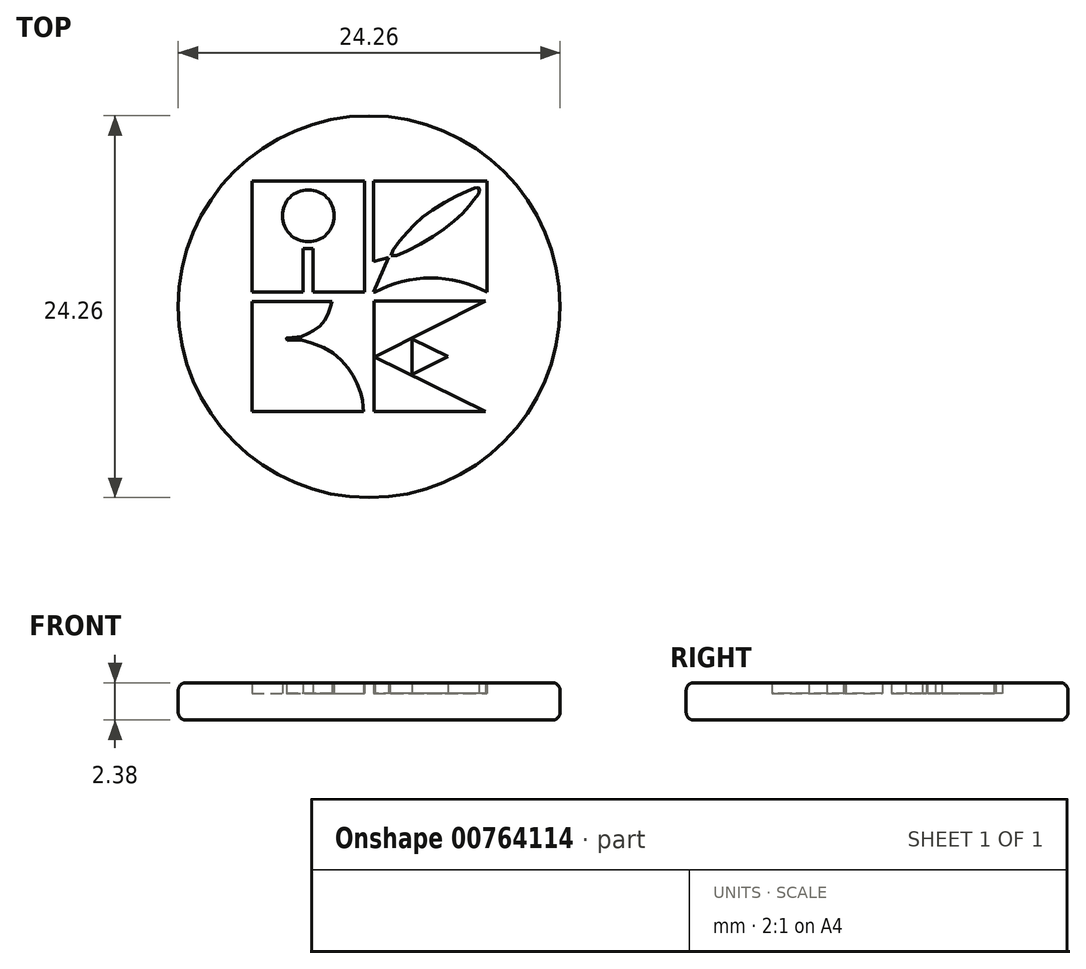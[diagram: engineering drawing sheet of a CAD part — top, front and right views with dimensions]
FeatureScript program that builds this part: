
annotation { "Feature Type Name" : "Feature", "Feature Type Description" : "" }
export const myFeature = defineFeature(function(context is Context, id is Id, definition is map)
    precondition{}
    {
        {
            assignVariable(context, id + "F0", {"name" : "SPES", "anyValue" : 2.38});
        }
        {
            var Q0;
            Q0=qCreatedBy(makeId("Top.planeOp"),FACE);
            var sketch = newSketch(context, id + "F1", { "sketchPlane" : qUnion([Q0])});
            skCircle(sketch, "E0", {"center": v(0, 0) * mm, "radius": 12.12 * mm});
            skLineSegment(sketch, "E1.bottom", {"start": v(-7.42, 7.97) * mm, "end": v(-0.28, 7.97) * mm});
            skLineSegment(sketch, "E1.top", {"start": v(-7.42, 0.93) * mm, "end": v(-4.19, 0.93) * mm});
            skLineSegment(sketch, "E1.left", {"start": v(-7.42, 7.97) * mm, "end": v(-7.42, 0.93) * mm});
            skLineSegment(sketch, "E1.right", {"start": v(-0.28, 7.97) * mm, "end": v(-0.28, 0.93) * mm});
            skLineSegment(sketch, "E2.bottom", {"start": v(-7.42, 0.33) * mm, "end": v(-0.28, 0.33) * mm});
            skLineSegment(sketch, "E2.top", {"start": v(-7.42, -6.67) * mm, "end": v(-0.28, -6.67) * mm});
            skLineSegment(sketch, "E2.left", {"start": v(-7.42, 0.33) * mm, "end": v(-7.42, -6.67) * mm});
            skLineSegment(sketch, "E2.right", {"start": v(-0.28, 0.33) * mm, "end": v(-0.28, -6.67) * mm});
            skLineSegment(sketch, "E3.bottom", {"start": v(0.3, 0.35) * mm, "end": v(7.4, 0.35) * mm});
            skLineSegment(sketch, "E3.top", {"start": v(0.3, -6.67) * mm, "end": v(7.4, -6.67) * mm});
            skLineSegment(sketch, "E3.left", {"start": v(0.3, 0.35) * mm, "end": v(0.3, -6.67) * mm});
            skLineSegment(sketch, "E3.right", {"start": v(7.4, 0.35) * mm, "end": v(7.4, -6.67) * mm});
            skLineSegment(sketch, "E4.bottom", {"start": v(0.28, 7.97) * mm, "end": v(7.48, 7.97) * mm});
            skLineSegment(sketch, "E4.top", {"start": v(0.28, 0.93) * mm, "end": v(7.48, 0.93) * mm});
            skLineSegment(sketch, "E4.left", {"start": v(0.28, 7.97) * mm, "end": v(0.28, 0.93) * mm});
            skLineSegment(sketch, "E4.right", {"start": v(7.48, 7.97) * mm, "end": v(7.48, 0.93) * mm});
            skCircle(sketch, "E5", {"center": v(-3.86, 5.78) * mm, "radius": 1.65 * mm});
            skPoint(sketch, "E5.first.point", {"position": v(-3.9, 7.42) * mm});
            skPoint(sketch, "E5.second.point", {"position": v(-2.22, 5.67) * mm});
            skPoint(sketch, "E5.third.point", {"position": v(-5.51, 5.72) * mm});
            skLineSegment(sketch, "E6.bottom", {"start": v(-4.19, 3.7) * mm, "end": v(-3.57, 3.7) * mm});
            skLineSegment(sketch, "E6.left", {"start": v(-4.19, 3.7) * mm, "end": v(-4.19, 0.93) * mm});
            skLineSegment(sketch, "E6.right", {"start": v(-3.57, 3.7) * mm, "end": v(-3.57, 0.93) * mm});
            skLineSegment(sketch, "E7.trimOffspring", {"start": v(-3.57, 0.93) * mm, "end": v(-0.28, 0.93) * mm});
            skLineSegment(sketch, "E8", {"start": v(-4.19, 0.93) * mm, "end": v(-3.57, 0.93) * mm});
            skLineSegment(sketch, "E9", {"start": v(7.4, 0.35) * mm, "end": v(0.35, -3.18) * mm});
            skLineSegment(sketch, "E10", {"start": v(0.35, -3.18) * mm, "end": v(7.4, -6.67) * mm});
            skLineSegment(sketch, "E11", {"start": v(2.73, -2.04) * mm, "end": v(2.73, -4.31) * mm});
            skLineSegment(sketch, "E12", {"start": v(2.73, -4.31) * mm, "end": v(5, -3.17) * mm});
            skLineSegment(sketch, "E13", {"start": v(5, -3.17) * mm, "end": v(2.73, -2.04) * mm});
            skFitSpline(sketch, "E14", {"points": [v(1.38, 3.27) * mm, v(2.23, 4.5) * mm, v(3.76, 5.97) * mm, v(6.37, 7.42) * mm, v(6.9, 7.57) * mm, v(6.96, 7.53) * mm, v(7.02, 7.38) * mm, v(6.73, 6.87) * mm, v(5.74, 5.75) * mm, v(3.16, 3.91) * mm, v(1.38, 3.27) * mm]});
            skArc(sketch, "E15", {"start": v(7.48, 0.93) * mm, "mid": v(3.92, 1.83) * mm, "end": v(0.36, 0.93) * mm});
            skLineSegment(sketch, "E16", {"start": v(0.28, 0.93) * mm, "end": v(1.22, 3.12) * mm});
            skLineSegment(sketch, "E17", {"start": v(1.22, 3.12) * mm, "end": v(0.28, 2.89) * mm});
            skFitSpline(sketch, "E18", {"points": [v(-2.37, 0.33) * mm, v(-2.47, -0.07) * mm, v(-2.6, -0.45) * mm, v(-2.9, -0.95) * mm, v(-3.19, -1.28) * mm, v(-3.7, -1.6) * mm, v(-4, -1.79) * mm, v(-4.67, -1.97) * mm, v(-5.24, -1.98) * mm, v(-5.25, -2.04) * mm, v(-5.23, -2.1) * mm, v(-5.15, -2.13) * mm, v(-4.74, -2.1) * mm, v(-4.18, -2.15) * mm, v(-2.83, -2.63) * mm, v(-1.92, -3.27) * mm, v(-1.2, -4.1) * mm, v(-0.83, -4.73) * mm, v(-0.5, -5.55) * mm, v(-0.41, -6.06) * mm, v(-0.36, -6.5) * mm, v(-0.35, -6.67) * mm], "startDerivative": vector(-2.3, -9.32) * mm, "endDerivative": vector(0.32, -5.36) * mm});
            skSolve(sketch);
        }
        {
            var Q0;
            Q0=makeQuery(id+"F1.imprint","IMPRINT",FACE,{"disambiguationData":[TD([[makeQuery(id+"F1.imprint","IMPRINT",EDGE,{"derivedFrom":sQuery(id+"F1.wireOp",EDGE,"E0")}),1.0]])]});
            extrude(context, id + "F2", {"entities" : qUnion([Q0]), "depth" : (getVariable(context, 'SPES')) * mm, "offsetDistance" : 25 * mm});
        }
        {
            var Q0;
            Q0=makeQuery(id+"F2.opExtrude","CAP_EDGE",EDGE,{"disambiguationData":[OSD([sQuery(id+"F1.wireOp",EDGE,"E0")])],"isStart":false});
            fillet(context, id + "F3", {"entities" : qUnion([Q0]), "radius" : 0.5 * mm, "tangentPropagation" : true, "allowEdgeOverflow" : false});
        }
        {
            var Q0;
            Q0=makeQuery(id+"F2.opExtrude","CAP_EDGE",EDGE,{"disambiguationData":[OSD([sQuery(id+"F1.wireOp",EDGE,"E0")])],"isStart":true});
            fillet(context, id + "F4", {"entities" : qUnion([Q0]), "radius" : 0.5 * mm, "tangentPropagation" : true, "allowEdgeOverflow" : false});
        }
        {
            var Q0;
            Q0=makeQuery(id+"F1.imprint","IMPRINT",FACE,{"disambiguationData":[TD([[makeQuery(id+"F1.imprint","IMPRINT",EDGE,{"derivedFrom":sQuery(id+"F1.wireOp",EDGE,"E6.bottom")}),-1.0]])]});
            var Q1;
            Q1=makeQuery(id+"F1.imprint","IMPRINT",FACE,{"disambiguationData":[TD([[makeQuery(id+"F1.imprint","IMPRINT",EDGE,{"derivedFrom":sQuery(id+"F1.wireOp",EDGE,"E1.bottom")}),-1.0]])]});
            var Q2;
            Q2=makeQuery(id+"F1.imprint","IMPRINT",FACE,{"disambiguationData":[TD([[makeQuery(id+"F1.imprint","IMPRINT",EDGE,{"derivedFrom":sQuery(id+"F1.wireOp",EDGE,"E5")}),1.0]])]});
            extrude(context, id + "F5", {"entities" : qUnion([Q0, Q1, Q2]), "operationType" : NewBodyOperationType.ADD, "depth" : 1.7 * mm, "offsetDistance" : 25 * mm});
        }
        {
            var Q0;
            Q0=makeQuery(id+"F1.imprint","IMPRINT",FACE,{"disambiguationData":[TD([[makeQuery(id+"F1.imprint","IMPRINT",EDGE,{"derivedFrom":sQuery(id+"F1.wireOp",EDGE,"E5")}),1.0]])]});
            var Q1;
            Q1=makeQuery(id+"F1.imprint","IMPRINT",FACE,{"disambiguationData":[TD([[makeQuery(id+"F1.imprint","IMPRINT",EDGE,{"derivedFrom":sQuery(id+"F1.wireOp",EDGE,"E6.bottom")}),-1.0]])]});
            var Q2;
            Q2=makeQuery(id+"F2.opExtrude","CAP_FACE",FACE,{"disambiguationData":[OSD([sQuery(id+"F1.wireOp",EDGE,"E0"),sQuery(id+"F1.wireOp",EDGE,"E1.bottom"),sQuery(id+"F1.wireOp",EDGE,"E1.top"),sQuery(id+"F1.wireOp",EDGE,"E1.left"),sQuery(id+"F1.wireOp",EDGE,"E1.right"),sQuery(id+"F1.wireOp",EDGE,"E2.bottom"),sQuery(id+"F1.wireOp",EDGE,"E2.top"),sQuery(id+"F1.wireOp",EDGE,"E2.left"),sQuery(id+"F1.wireOp",EDGE,"E2.right"),sQuery(id+"F1.wireOp",EDGE,"E3.bottom"),sQuery(id+"F1.wireOp",EDGE,"E3.top"),sQuery(id+"F1.wireOp",EDGE,"E3.left"),sQuery(id+"F1.wireOp",EDGE,"E3.right"),sQuery(id+"F1.wireOp",EDGE,"E4.bottom"),sQuery(id+"F1.wireOp",EDGE,"E4.top"),sQuery(id+"F1.wireOp",EDGE,"E4.left"),sQuery(id+"F1.wireOp",EDGE,"E4.right"),sQuery(id+"F1.wireOp",EDGE,"E7.trimOffspring"),sQuery(id+"F1.wireOp",EDGE,"E8")])],"isStart":false});
            extrude(context, id + "F6", {"entities" : qUnion([Q0, Q1]), "operationType" : NewBodyOperationType.ADD, "endBound" : BoundingType.UP_TO_SURFACE, "depth" : 2 * mm, "endBoundEntityFace" : qUnion([Q2]), "offsetDistance" : 25 * mm});
        }
        {
            var Q0;
            {var subQ0=sQuery(id+"F1.wireOp",EDGE,"E3.bottom");Q0=makeQuery(id+"F1.imprint","IMPRINT",FACE,{"disambiguationData":[TD([[makeQuery(id+"F1.imprint","IMPRINT",EDGE,{"derivedFrom":subQ0}),-1.0]])]});}
            var Q1;
            {var subQ1=sQuery(id+"F1.wireOp",EDGE,"E3.right");Q1=makeQuery(id+"F1.imprint","IMPRINT",FACE,{"disambiguationData":[TD([[makeQuery(id+"F1.imprint","IMPRINT",EDGE,{"derivedFrom":subQ1}),-1.0]])]});}
            var Q2;
            Q2=makeQuery(id+"F1.imprint","IMPRINT",FACE,{"disambiguationData":[TD([[makeQuery(id+"F1.imprint","IMPRINT",EDGE,{"derivedFrom":sQuery(id+"F1.wireOp",EDGE,"IOD86GQd-rjmQ-qHtz-Bk1f-0n8stFa7D3gi")}),1.0]])]});
            var Q3;
            {var subQ0=sQuery(id+"F1.wireOp",EDGE,"E3.top");Q3=makeQuery(id+"F1.imprint","IMPRINT",FACE,{"disambiguationData":[TD([[makeQuery(id+"F1.imprint","IMPRINT",EDGE,{"derivedFrom":subQ0}),1.0]])]});}
            var Q4;
            {var subQ3=sQuery(id+"F1.wireOp",EDGE,"IOD86GQd-rjmQ-qHtz-Bk1f-0n8stFa7D3gi");Q4=makeQuery(id+"F1.imprint","IMPRINT",FACE,{"disambiguationData":[TD([[makeQuery(id+"F1.imprint","IMPRINT",EDGE,{"derivedFrom":subQ3}),-1.0]])]});}
            var Q5;
            Q5=makeQuery(id+"F1.imprint","IMPRINT",FACE,{"disambiguationData":[TD([[makeQuery(id+"F1.imprint","IMPRINT",EDGE,{"derivedFrom":sQuery(id+"F1.wireOp",EDGE,"E11")}),1.0]])]});
            extrude(context, id + "F7", {"entities" : qUnion([Q0, Q1, Q2, Q3, Q4, Q5]), "operationType" : NewBodyOperationType.ADD, "depth" : 1.7 * mm, "offsetDistance" : 25 * mm});
        }
        {
            var Q0;
            Q0=makeQuery(id+"F1.imprint","IMPRINT",FACE,{"disambiguationData":[TD([[makeQuery(id+"F1.imprint","IMPRINT",EDGE,{"derivedFrom":sQuery(id+"F1.wireOp",EDGE,"E3.right")}),-1.0]])]});
            var Q1;
            {var subQ0=sQuery(id+"F1.wireOp",EDGE,"E8");var subQ1=sQuery(id+"F1.wireOp",EDGE,"E7.trimOffspring");var subQ2=sQuery(id+"F1.wireOp",EDGE,"E4.right");var subQ3=sQuery(id+"F1.wireOp",EDGE,"E4.left");var subQ4=sQuery(id+"F1.wireOp",EDGE,"E4.top");var subQ5=sQuery(id+"F1.wireOp",EDGE,"E4.bottom");var subQ6=sQuery(id+"F1.wireOp",EDGE,"E3.right");var subQ7=sQuery(id+"F1.wireOp",EDGE,"E3.left");var subQ8=sQuery(id+"F1.wireOp",EDGE,"E3.top");var subQ9=sQuery(id+"F1.wireOp",EDGE,"E3.bottom");var subQ10=sQuery(id+"F1.wireOp",EDGE,"E2.right");var subQ11=sQuery(id+"F1.wireOp",EDGE,"E2.left");var subQ12=sQuery(id+"F1.wireOp",EDGE,"E2.top");var subQ13=sQuery(id+"F1.wireOp",EDGE,"E2.bottom");var subQ14=sQuery(id+"F1.wireOp",EDGE,"E1.right");var subQ15=sQuery(id+"F1.wireOp",EDGE,"E1.left");var subQ16=sQuery(id+"F1.wireOp",EDGE,"E1.top");var subQ17=sQuery(id+"F1.wireOp",EDGE,"E1.bottom");var subQ18=sQuery(id+"F1.wireOp",EDGE,"E0");Q1=makeQuery(id+"F6.boolean.opBoolean","MERGE",FACE,{"derivedFrom":[makeQuery(id+"F2.opExtrude","CAP_FACE",FACE,{"disambiguationData":[OSD([subQ18,subQ17,subQ16,subQ15,subQ14,subQ13,subQ12,subQ11,subQ10,subQ9,subQ8,subQ7,subQ6,subQ5,subQ4,subQ3,subQ2,subQ1,subQ0])],"isStart":false}),makeQuery(id+"F6.opExtrude","CAP_FACE",FACE,{"disambiguationData":[OSD([subQ18,subQ17,subQ16,subQ15,subQ14,subQ13,subQ12,subQ11,subQ10,subQ9,subQ8,subQ7,subQ6,subQ5,subQ4,subQ3,subQ2,subQ1,subQ0]),OD(1.0)],"isStart":false})]});}
            extrude(context, id + "F8", {"entities" : qUnion([Q0]), "operationType" : NewBodyOperationType.ADD, "endBound" : BoundingType.UP_TO_SURFACE, "depth" : 2 * mm, "endBoundEntityFace" : qUnion([Q1]), "offsetDistance" : 25 * mm});
        }
        {
            var Q0;
            Q0=makeQuery(id+"F1.imprint","IMPRINT",FACE,{"disambiguationData":[TD([[makeQuery(id+"F1.imprint","IMPRINT",EDGE,{"derivedFrom":sQuery(id+"F1.wireOp",EDGE,"E14")}),-1.0]])]});
            var Q1;
            {var subQ1=sQuery(id+"F1.wireOp",EDGE,"E4.bottom");Q1=makeQuery(id+"F1.imprint","IMPRINT",FACE,{"disambiguationData":[TD([[makeQuery(id+"F1.imprint","IMPRINT",EDGE,{"derivedFrom":subQ1}),-1.0]])]});}
            var Q2;
            {var subQ0=sQuery(id+"F1.wireOp",EDGE,"CtFy2ePs-kT9T-Hoj8-najl-6mpfo2gU634l");Q2=makeQuery(id+"F1.imprint","IMPRINT",FACE,{"disambiguationData":[TD([[makeQuery(id+"F1.imprint","IMPRINT",EDGE,{"derivedFrom":subQ0}),-1.0]])]});}
            var Q3;
            Q3=makeQuery(id+"F1.imprint","IMPRINT",FACE,{"disambiguationData":[TD([[makeQuery(id+"F1.imprint","IMPRINT",EDGE,{"derivedFrom":sQuery(id+"F1.wireOp",EDGE,"E4.top")}),1.0]])]});
            var Q4;
            {var subQ0=sQuery(id+"F1.wireOp",EDGE,"E16");Q4=makeQuery(id+"F1.imprint","IMPRINT",FACE,{"disambiguationData":[TD([[makeQuery(id+"F1.imprint","IMPRINT",EDGE,{"derivedFrom":subQ0}),1.0]])]});}
            extrude(context, id + "F9", {"entities" : qUnion([Q0, Q1, Q2, Q3, Q4]), "operationType" : NewBodyOperationType.ADD, "depth" : 1.7 * mm, "offsetDistance" : 25 * mm});
        }
        {
            var Q0;
            {var subQ0=sQuery(id+"F1.wireOp",EDGE,"E16");Q0=makeQuery(id+"F1.imprint","IMPRINT",FACE,{"disambiguationData":[TD([[makeQuery(id+"F1.imprint","IMPRINT",EDGE,{"derivedFrom":subQ0}),1.0]])]});}
            var Q1;
            {var subQ0=sQuery(id+"F1.wireOp",EDGE,"E15");Q1=makeQuery(id+"F1.imprint","IMPRINT",FACE,{"disambiguationData":[TD([[makeQuery(id+"F1.imprint","IMPRINT",EDGE,{"derivedFrom":subQ0}),1.0]])]});}
            var Q2;
            Q2=makeQuery(id+"F1.imprint","IMPRINT",FACE,{"disambiguationData":[TD([[makeQuery(id+"F1.imprint","IMPRINT",EDGE,{"derivedFrom":sQuery(id+"F1.wireOp",EDGE,"E14")}),-1.0]])]});
            var Q3;
            {var subQ0=sQuery(id+"F1.wireOp",EDGE,"E8");var subQ1=sQuery(id+"F1.wireOp",EDGE,"E7.trimOffspring");var subQ2=sQuery(id+"F1.wireOp",EDGE,"E4.right");var subQ3=sQuery(id+"F1.wireOp",EDGE,"E4.left");var subQ4=sQuery(id+"F1.wireOp",EDGE,"E4.top");var subQ5=sQuery(id+"F1.wireOp",EDGE,"E4.bottom");var subQ6=sQuery(id+"F1.wireOp",EDGE,"E3.right");var subQ7=sQuery(id+"F1.wireOp",EDGE,"E3.left");var subQ8=sQuery(id+"F1.wireOp",EDGE,"E3.top");var subQ9=sQuery(id+"F1.wireOp",EDGE,"E3.bottom");var subQ10=sQuery(id+"F1.wireOp",EDGE,"E2.right");var subQ11=sQuery(id+"F1.wireOp",EDGE,"E2.left");var subQ12=sQuery(id+"F1.wireOp",EDGE,"E2.top");var subQ13=sQuery(id+"F1.wireOp",EDGE,"E2.bottom");var subQ14=sQuery(id+"F1.wireOp",EDGE,"E1.right");var subQ15=sQuery(id+"F1.wireOp",EDGE,"E1.left");var subQ16=sQuery(id+"F1.wireOp",EDGE,"E1.top");var subQ17=sQuery(id+"F1.wireOp",EDGE,"E1.bottom");var subQ18=sQuery(id+"F1.wireOp",EDGE,"E0");Q3=makeQuery(id+"F8.boolean.opBoolean","MERGE",FACE,{"derivedFrom":[makeQuery(id+"F6.boolean.opBoolean","MERGE",FACE,{"derivedFrom":[makeQuery(id+"F2.opExtrude","CAP_FACE",FACE,{"disambiguationData":[OSD([subQ18,subQ17,subQ16,subQ15,subQ14,subQ13,subQ12,subQ11,subQ10,subQ9,subQ8,subQ7,subQ6,subQ5,subQ4,subQ3,subQ2,subQ1,subQ0])],"isStart":false}),makeQuery(id+"F6.opExtrude","CAP_FACE",FACE,{"disambiguationData":[OSD([subQ18,subQ17,subQ16,subQ15,subQ14,subQ13,subQ12,subQ11,subQ10,subQ9,subQ8,subQ7,subQ6,subQ5,subQ4,subQ3,subQ2,subQ1,subQ0]),OD(1.0)],"isStart":false})]}),makeQuery(id+"F8.opExtrude","CAP_FACE",FACE,{"disambiguationData":[OSD([subQ18,subQ17,subQ16,subQ15,subQ14,subQ13,subQ12,subQ11,subQ10,subQ9,subQ8,subQ7,subQ6,subQ5,subQ4,subQ3,subQ2,subQ1,subQ0])],"isStart":false})]});}
            extrude(context, id + "F10", {"entities" : qUnion([Q0, Q1, Q2]), "operationType" : NewBodyOperationType.ADD, "endBound" : BoundingType.UP_TO_SURFACE, "depth" : 2 * mm, "endBoundEntityFace" : qUnion([Q3]), "offsetDistance" : 25 * mm});
        }
        {
            var Q0;
            {var subQ0=sQuery(id+"F1.wireOp",EDGE,"E2.left");Q0=makeQuery(id+"F1.imprint","IMPRINT",FACE,{"disambiguationData":[TD([[makeQuery(id+"F1.imprint","IMPRINT",EDGE,{"derivedFrom":subQ0}),1.0]])]});}
            var Q1;
            {var subQ0=sQuery(id+"F1.wireOp",EDGE,"E2.right");Q1=makeQuery(id+"F1.imprint","IMPRINT",FACE,{"disambiguationData":[TD([[makeQuery(id+"F1.imprint","IMPRINT",EDGE,{"derivedFrom":subQ0}),-1.0]])]});}
            extrude(context, id + "F11", {"entities" : qUnion([Q0, Q1]), "operationType" : NewBodyOperationType.ADD, "depth" : 1.7 * mm, "offsetDistance" : 25 * mm});
        }
        {
            var Q0;
            {var subQ0=sQuery(id+"F1.wireOp",EDGE,"E2.right");Q0=makeQuery(id+"F1.imprint","IMPRINT",FACE,{"disambiguationData":[TD([[makeQuery(id+"F1.imprint","IMPRINT",EDGE,{"derivedFrom":subQ0}),-1.0]])]});}
            var Q1;
            {var subQ0=sQuery(id+"F1.wireOp",EDGE,"E8");var subQ1=sQuery(id+"F1.wireOp",EDGE,"E7.trimOffspring");var subQ2=sQuery(id+"F1.wireOp",EDGE,"E4.right");var subQ3=sQuery(id+"F1.wireOp",EDGE,"E4.left");var subQ4=sQuery(id+"F1.wireOp",EDGE,"E4.top");var subQ5=sQuery(id+"F1.wireOp",EDGE,"E4.bottom");var subQ6=sQuery(id+"F1.wireOp",EDGE,"E3.right");var subQ7=sQuery(id+"F1.wireOp",EDGE,"E3.left");var subQ8=sQuery(id+"F1.wireOp",EDGE,"E3.top");var subQ9=sQuery(id+"F1.wireOp",EDGE,"E3.bottom");var subQ10=sQuery(id+"F1.wireOp",EDGE,"E2.right");var subQ11=sQuery(id+"F1.wireOp",EDGE,"E2.left");var subQ12=sQuery(id+"F1.wireOp",EDGE,"E2.top");var subQ13=sQuery(id+"F1.wireOp",EDGE,"E2.bottom");var subQ14=sQuery(id+"F1.wireOp",EDGE,"E1.right");var subQ15=sQuery(id+"F1.wireOp",EDGE,"E1.left");var subQ16=sQuery(id+"F1.wireOp",EDGE,"E1.top");var subQ17=sQuery(id+"F1.wireOp",EDGE,"E1.bottom");var subQ18=sQuery(id+"F1.wireOp",EDGE,"E0");Q1=makeQuery(id+"F10.boolean.opBoolean","MERGE",FACE,{"derivedFrom":[makeQuery(id+"F8.boolean.opBoolean","MERGE",FACE,{"derivedFrom":[makeQuery(id+"F6.boolean.opBoolean","MERGE",FACE,{"derivedFrom":[makeQuery(id+"F2.opExtrude","CAP_FACE",FACE,{"disambiguationData":[OSD([subQ18,subQ17,subQ16,subQ15,subQ14,subQ13,subQ12,subQ11,subQ10,subQ9,subQ8,subQ7,subQ6,subQ5,subQ4,subQ3,subQ2,subQ1,subQ0])],"isStart":false}),makeQuery(id+"F6.opExtrude","CAP_FACE",FACE,{"disambiguationData":[OSD([subQ18,subQ17,subQ16,subQ15,subQ14,subQ13,subQ12,subQ11,subQ10,subQ9,subQ8,subQ7,subQ6,subQ5,subQ4,subQ3,subQ2,subQ1,subQ0]),OD(1.0)],"isStart":false})]}),makeQuery(id+"F8.opExtrude","CAP_FACE",FACE,{"disambiguationData":[OSD([subQ18,subQ17,subQ16,subQ15,subQ14,subQ13,subQ12,subQ11,subQ10,subQ9,subQ8,subQ7,subQ6,subQ5,subQ4,subQ3,subQ2,subQ1,subQ0])],"isStart":false})]}),makeQuery(id+"F10.opExtrude","CAP_FACE",FACE,{"disambiguationData":[OSD([subQ18,subQ17,subQ16,subQ15,subQ14,subQ13,subQ12,subQ11,subQ10,subQ9,subQ8,subQ7,subQ6,subQ5,subQ4,subQ3,subQ2,subQ1,subQ0]),OD(0.0)],"isStart":false}),makeQuery(id+"F10.opExtrude","CAP_FACE",FACE,{"disambiguationData":[OSD([subQ18,subQ17,subQ16,subQ15,subQ14,subQ13,subQ12,subQ11,subQ10,subQ9,subQ8,subQ7,subQ6,subQ5,subQ4,subQ3,subQ2,subQ1,subQ0]),OD(1.0)],"isStart":false})]});}
            extrude(context, id + "F12", {"entities" : qUnion([Q0]), "operationType" : NewBodyOperationType.ADD, "endBound" : BoundingType.UP_TO_SURFACE, "depth" : 2 * mm, "endBoundEntityFace" : qUnion([Q1]), "offsetDistance" : 25 * mm});
        }
    });
